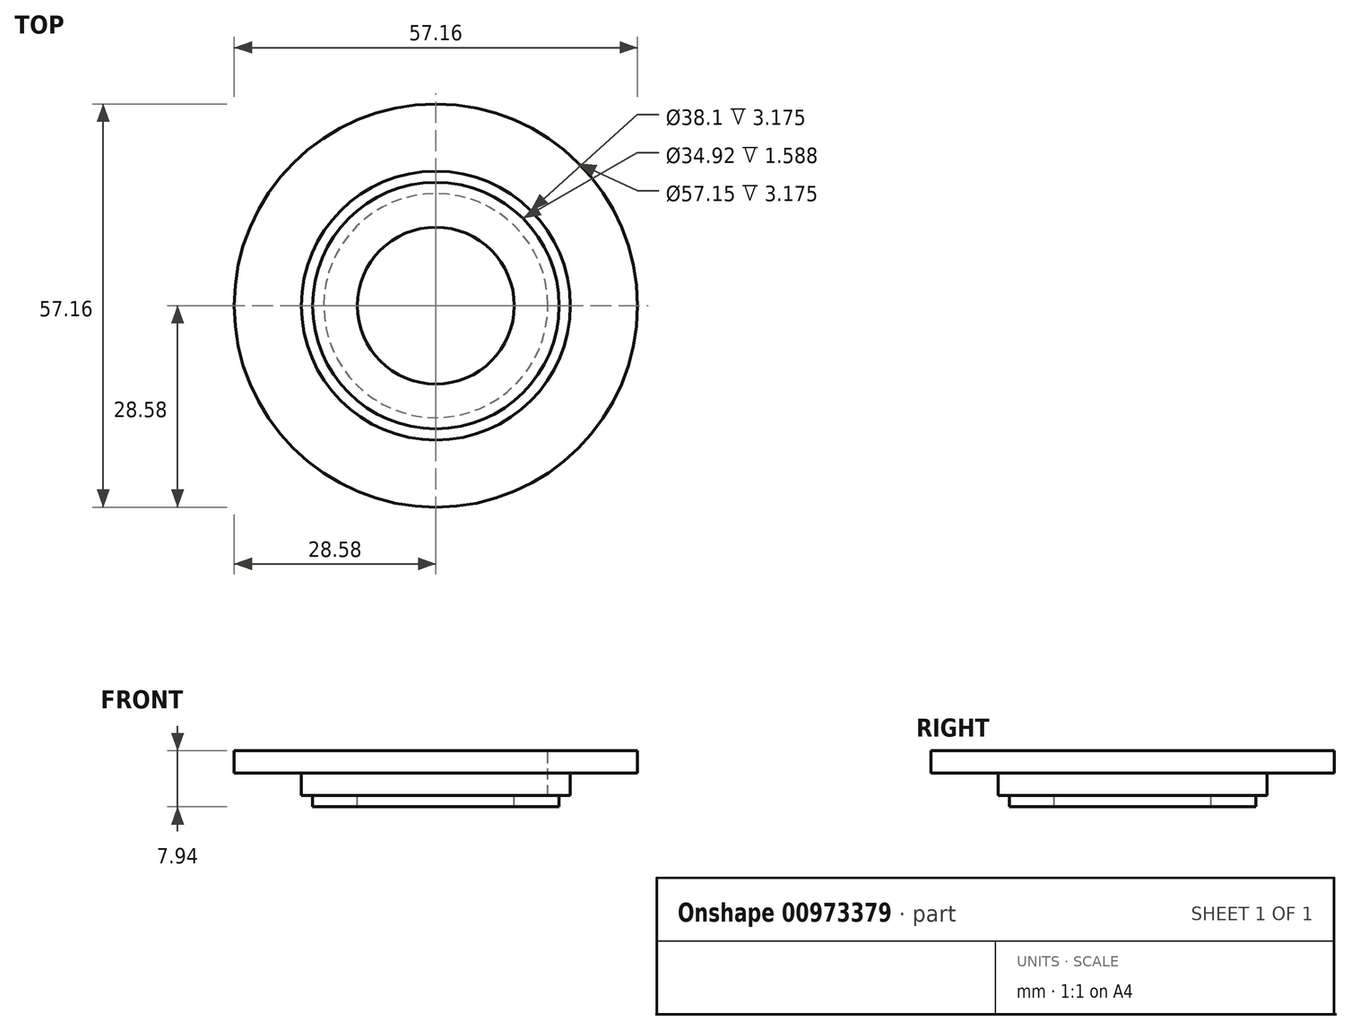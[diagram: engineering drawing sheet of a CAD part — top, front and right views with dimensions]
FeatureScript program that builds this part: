
annotation { "Feature Type Name" : "Feature", "Feature Type Description" : "" }
export const myFeature = defineFeature(function(context is Context, id is Id, definition is map)
    precondition{}
    {
        {
            var Q0;
            Q0=qCreatedBy(makeId("Front.planeOp"),FACE);
            var sketch = newSketch(context, id + "F0", { "sketchPlane" : qUnion([Q0])});
            skLineSegment(sketch, "E0", {"start": v(0, 0) * mm, "end": v(0, 53.06) * mm, "construction": true});
            skLineSegment(sketch, "E1", {"start": v(4.76, 0) * mm, "end": v(4.76, 1.59) * mm, "construction": true});
            skLineSegment(sketch, "E2", {"start": v(4.76, 0) * mm, "end": v(15.88, 0) * mm, "construction": true});
            skLineSegment(sketch, "E3", {"start": v(4.76, 1.59) * mm, "end": v(26.2, 1.59) * mm, "construction": true});
            skLineSegment(sketch, "E4", {"start": v(26.2, 3.97) * mm, "end": v(26.2, 1.59) * mm, "construction": true});
            skLineSegment(sketch, "E5", {"start": v(26.2, 3.97) * mm, "end": v(31.75, 3.97) * mm, "construction": true});
            skLineSegment(sketch, "E6", {"start": v(17.46, 19.85) * mm, "end": v(11.11, 19.85) * mm});
            skLineSegment(sketch, "E7", {"start": v(11.11, 19.85) * mm, "end": v(11.11, 21.44) * mm});
            skLineSegment(sketch, "E8", {"start": v(17.46, 21.44) * mm, "end": v(17.46, 19.85) * mm});
            skLineSegment(sketch, "E9", {"start": v(19.05, 24.61) * mm, "end": v(28.58, 24.61) * mm});
            skLineSegment(sketch, "E10", {"start": v(28.58, 24.61) * mm, "end": v(28.58, 27.79) * mm});
            skLineSegment(sketch, "E11", {"start": v(28.58, 27.79) * mm, "end": v(15.88, 27.79) * mm});
            skLineSegment(sketch, "E12", {"start": v(15.88, 27.79) * mm, "end": v(15.88, 21.44) * mm});
            skLineSegment(sketch, "E13", {"start": v(15.88, 21.44) * mm, "end": v(11.11, 21.44) * mm});
            skLineSegment(sketch, "E14", {"start": v(31.75, 3.97) * mm, "end": v(31.75, 0) * mm, "construction": true});
            skLineSegment(sketch, "E15", {"start": v(15.88, 0) * mm, "end": v(15.88, -4.76) * mm, "construction": true});
            skLineSegment(sketch, "E16", {"start": v(15.88, -4.76) * mm, "end": v(11.11, -4.76) * mm, "construction": true});
            skLineSegment(sketch, "E17", {"start": v(11.11, -4.76) * mm, "end": v(11.11, -6.35) * mm, "construction": true});
            skLineSegment(sketch, "E18.trimOffspring", {"start": v(17.46, 0) * mm, "end": v(31.75, 0) * mm, "construction": true});
            skLineSegment(sketch, "E19", {"start": v(11.11, -6.35) * mm, "end": v(19.94, -6.35) * mm, "construction": true});
            skLineSegment(sketch, "E20", {"start": v(19.94, -19.05) * mm, "end": v(21.53, -19.05) * mm, "construction": true});
            skLineSegment(sketch, "E21", {"start": v(19.94, -19.05) * mm, "end": v(19.94, -6.35) * mm, "construction": true});
            skLineSegment(sketch, "E22", {"start": v(17.46, 0) * mm, "end": v(17.46, -4.76) * mm, "construction": true});
            skLineSegment(sketch, "E23", {"start": v(17.46, -4.76) * mm, "end": v(21.53, -4.76) * mm, "construction": true});
            skLineSegment(sketch, "E24", {"start": v(21.53, -4.76) * mm, "end": v(21.53, -19.05) * mm, "construction": true});
            skPoint(sketch, "E25.orphan", {"position": v(30.16, 3.97) * mm});
            skPoint(sketch, "E26.orphan", {"position": v(15.88, 19.85) * mm});
            skLineSegment(sketch, "E27", {"start": v(17.46, 21.44) * mm, "end": v(19.05, 21.44) * mm});
            skLineSegment(sketch, "E28", {"start": v(19.05, 21.44) * mm, "end": v(19.05, 24.61) * mm});
            skSolve(sketch);
        }
        {
            var Q0;
            Q0=qConstructionFilter(qBodyType(qCreatedBy(id+"F0",EDGE),BodyType.WIRE),ConstructionObject.NO);
            var Q1;
            Q1=sQuery(id+"F0.wireOp",EDGE,"E0");
            revolve(context, id + "F1", {"bodyType" : ToolBodyType.SURFACE, "surfaceOperationType" : NewSurfaceOperationType.NEW, "surfaceEntities" : qUnion([Q0]), "axis" : qUnion([Q1]), "revolveType" : RevolveType.FULL});
        }
    });
